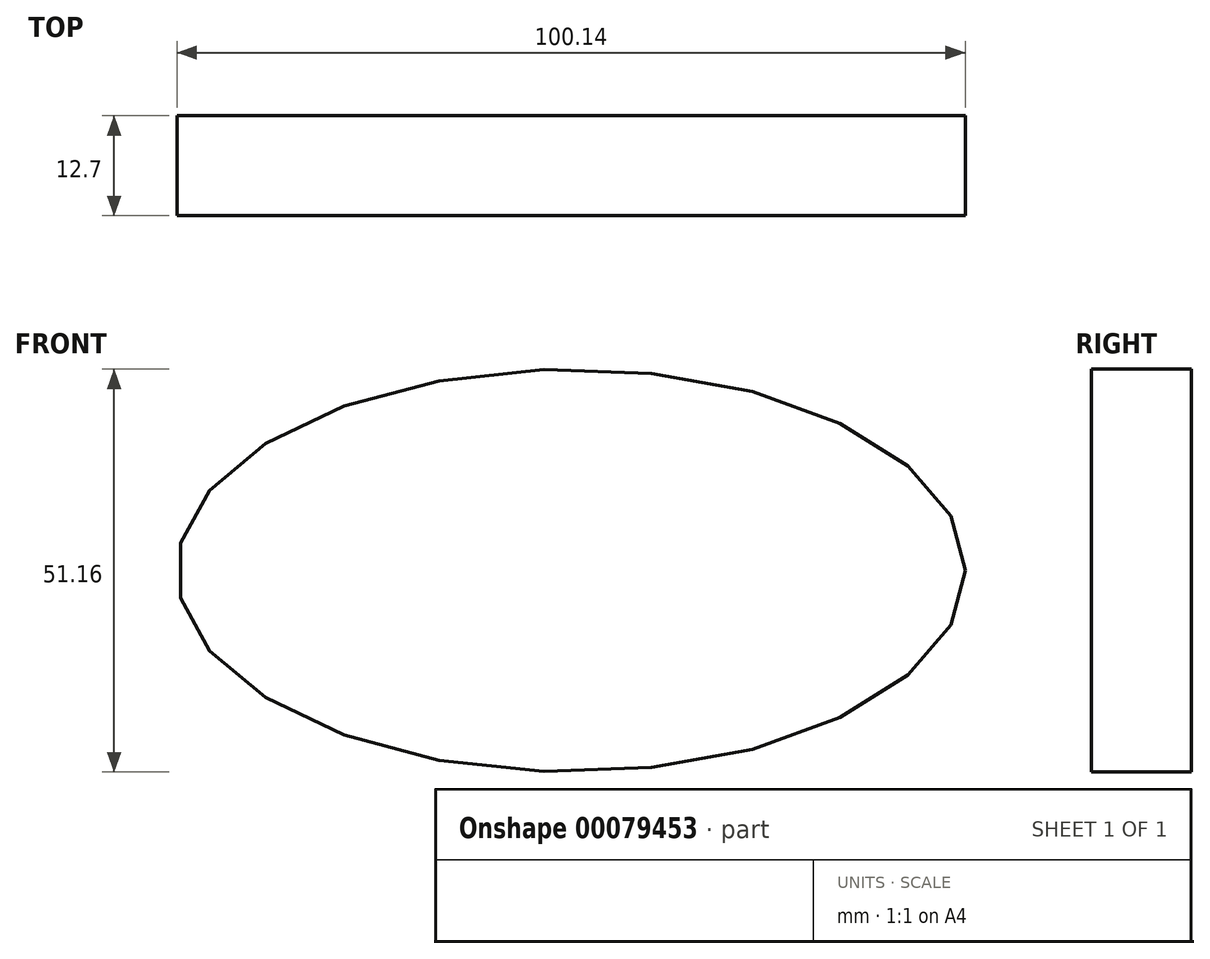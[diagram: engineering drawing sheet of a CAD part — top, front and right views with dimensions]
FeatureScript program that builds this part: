
annotation { "Feature Type Name" : "Feature", "Feature Type Description" : "" }
export const myFeature = defineFeature(function(context is Context, id is Id, definition is map)
    precondition{}
    {
        {
            var Q0;
            Q0=qCreatedBy(makeId("Front.planeOp"),FACE);
            var sketch = newSketch(context, id + "F0", { "sketchPlane" : qUnion([Q0])});
            skLineSegment(sketch, "E0", {"start": v(-51.53, 20.96) * mm, "end": v(-50.07, 20.96) * mm});
            skEllipse(sketch, "E1", {"center": v(0, 20.96) * mm, "majorRadius": 50.07 * mm, "minorRadius": 25.58 * mm, "majorAxis": v(1, 0)});
            skPoint(sketch, "E1.centerSnap0", {"position": v(-0.73, 20.96) * mm});
            skLineSegment(sketch, "E2.trimOffspring", {"start": v(-0.73, 20.96) * mm, "end": v(0, 20.96) * mm});
            skPoint(sketch, "E3.orphan", {"position": v(50.07, 20.96) * mm});
            skFitSpline(sketch, "E4.0", {"points": [v(43.64, 19.65) * mm, v(43.76, 20.96) * mm, v(43.64, 22.26) * mm, v(43.24, 23.64) * mm, v(42.51, 25.13) * mm, v(41.4, 26.74) * mm, v(39.86, 28.41) * mm, v(37.87, 30.11) * mm, v(35.85, 31.51) * mm, v(34.02, 32.6) * mm, v(32.53, 33.4) * mm, v(30.95, 34.16) * mm, v(28.74, 35.14) * mm, v(25.78, 36.26) * mm, v(21.95, 37.43) * mm, v(17.88, 38.4) * mm, v(13.61, 39.2) * mm, v(9.19, 39.76) * mm, v(5.4, 40.05) * mm, v(2.33, 40.17) * mm, v(0, 40.2) * mm, v(-2.33, 40.17) * mm, v(-5.4, 40.05) * mm, v(-9.19, 39.76) * mm, v(-13.61, 39.2) * mm, v(-17.88, 38.4) * mm, v(-21.95, 37.43) * mm, v(-25.78, 36.26) * mm, v(-28.74, 35.14) * mm, v(-30.95, 34.16) * mm, v(-32.53, 33.4) * mm, v(-34.02, 32.6) * mm, v(-35.85, 31.51) * mm, v(-37.87, 30.11) * mm, v(-39.86, 28.41) * mm, v(-41.4, 26.74) * mm, v(-42.51, 25.13) * mm, v(-43.24, 23.64) * mm, v(-43.64, 22.26) * mm, v(-43.76, 20.96) * mm, v(-43.64, 19.65) * mm, v(-43.24, 18.28) * mm, v(-42.51, 16.79) * mm, v(-41.4, 15.18) * mm, v(-39.86, 13.5) * mm, v(-37.87, 11.8) * mm, v(-35.85, 10.4) * mm, v(-34.02, 9.32) * mm, v(-32.53, 8.52) * mm, v(-30.95, 7.76) * mm, v(-28.74, 6.78) * mm, v(-25.78, 5.66) * mm, v(-21.95, 4.5) * mm, v(-17.88, 3.5) * mm, v(-13.61, 2.73) * mm, v(-9.19, 2.16) * mm, v(-5.4, 1.87) * mm, v(-2.33, 1.75) * mm, v(0, 1.72) * mm, v(2.33, 1.75) * mm, v(5.4, 1.87) * mm, v(9.19, 2.16) * mm, v(13.61, 2.73) * mm, v(17.88, 3.5) * mm, v(21.95, 4.5) * mm, v(25.78, 5.66) * mm, v(28.74, 6.78) * mm, v(30.95, 7.76) * mm, v(32.53, 8.52) * mm, v(34.02, 9.32) * mm, v(35.85, 10.4) * mm, v(37.87, 11.8) * mm, v(39.86, 13.5) * mm, v(41.4, 15.18) * mm, v(42.51, 16.79) * mm, v(43.24, 18.28) * mm, v(43.64, 19.65) * mm, v(43.76, 20.96) * mm, v(43.64, 22.26) * mm, v(43.64, 19.65) * mm]});
            skSolve(sketch);
        }
        {
            var Q0;
            Q0 = qSketchRegion(id + "F0", true);
            extrude(context, id + "F1", {"entities" : qUnion([Q0]), "depth" : 12.7 * mm});
        }
    });
